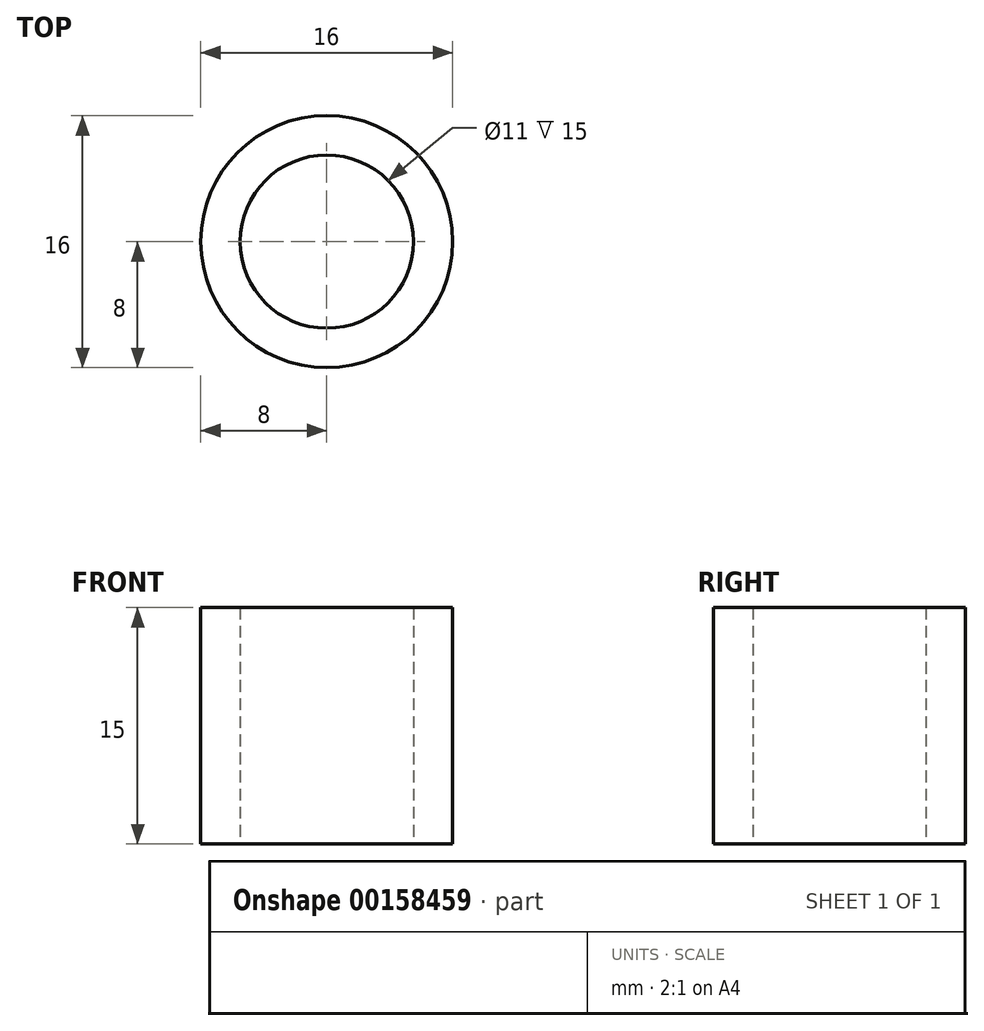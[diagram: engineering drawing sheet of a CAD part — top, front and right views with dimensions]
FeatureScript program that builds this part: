
annotation { "Feature Type Name" : "Feature", "Feature Type Description" : "" }
export const myFeature = defineFeature(function(context is Context, id is Id, definition is map)
    precondition{}
    {
        {
            var Q0;
            Q0=qCreatedBy(makeId("Top.planeOp"),FACE);
            var sketch = newSketch(context, id + "F0", { "sketchPlane" : qUnion([Q0])});
            skCircle(sketch, "E0", {"center": v(0, 0) * mm, "radius": 5.5 * mm});
            skCircle(sketch, "E1", {"center": v(0, 0) * mm, "radius": 8 * mm});
            skSolve(sketch);
        }
        {
            var Q0;
            Q0 = qSketchRegion(id + "F0", true);
            var Q1;
            Q1=makeQuery(id+"F0.imprint","IMPRINT",FACE,{"disambiguationData":[TD([[makeQuery(id+"F0.imprint","IMPRINT",EDGE,{"derivedFrom":sQuery(id+"F0.wireOp",EDGE,"E0")}),-1.0]])]});
            extrude(context, id + "F1", {"entities" : qUnion([Q0, Q1]), "depth" : 15 * mm});
        }
    });
